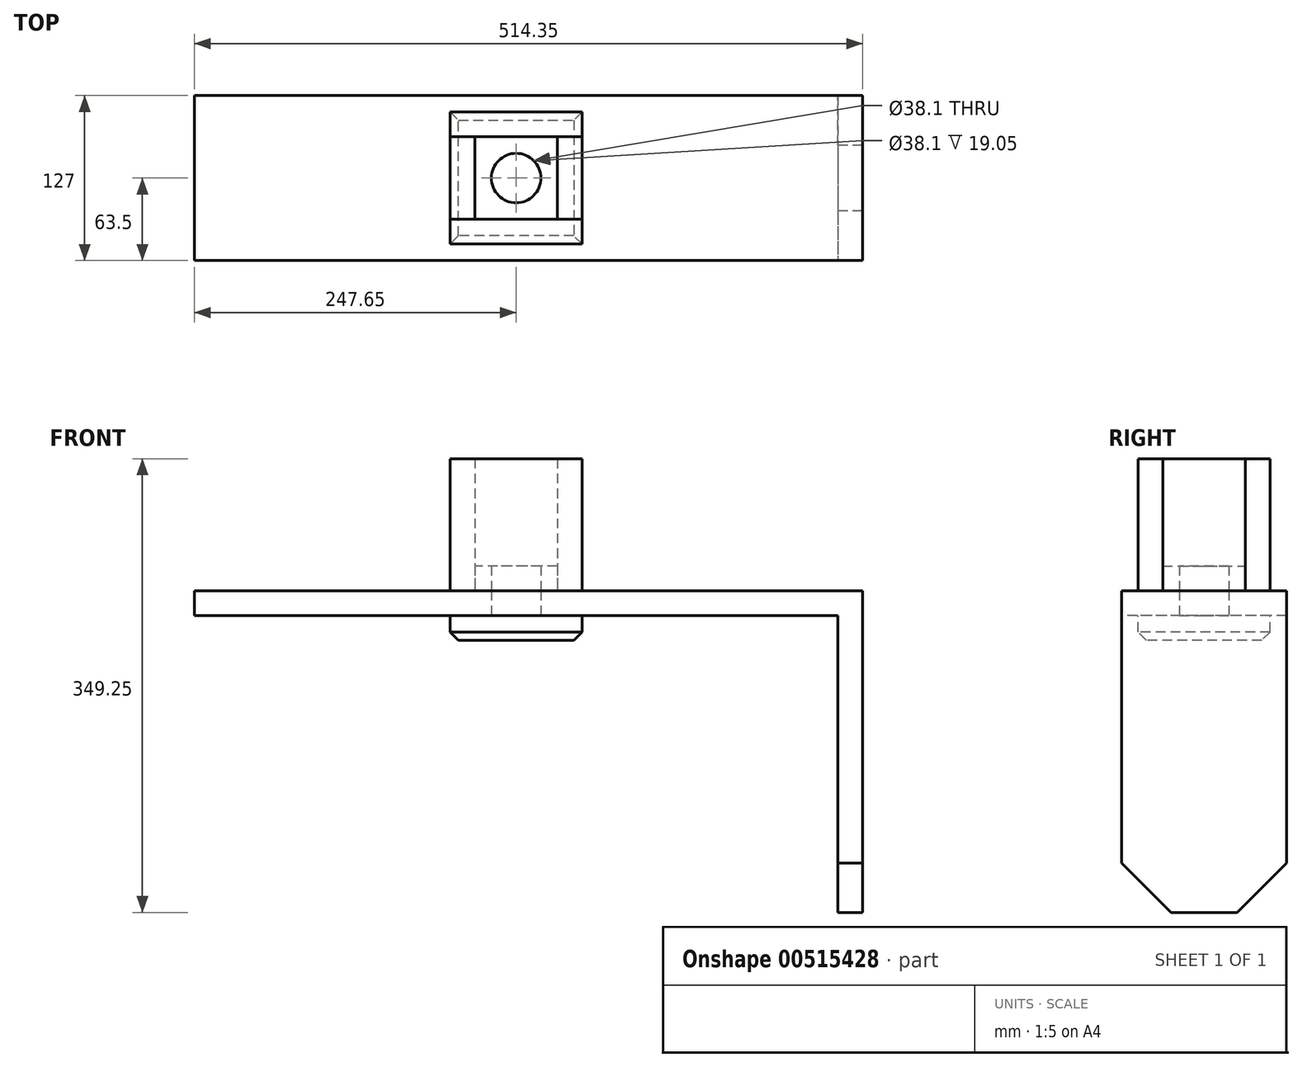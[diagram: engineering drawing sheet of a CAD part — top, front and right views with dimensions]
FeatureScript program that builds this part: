
annotation { "Feature Type Name" : "Feature", "Feature Type Description" : "" }
export const myFeature = defineFeature(function(context is Context, id is Id, definition is map)
    precondition{}
    {
        {
            var Q0;
            Q0=qCreatedBy(makeId("Top.planeOp"),FACE);
            var sketch = newSketch(context, id + "F0", { "sketchPlane" : qUnion([Q0])});
            skLineSegment(sketch, "E0.bottom", {"start": v(266.7, -63.5) * mm, "end": v(-266.7, -63.5) * mm});
            skLineSegment(sketch, "E0.top", {"start": v(266.7, 63.5) * mm, "end": v(-266.7, 63.5) * mm});
            skLineSegment(sketch, "E0.left", {"start": v(266.7, -63.5) * mm, "end": v(266.7, 63.5) * mm});
            skLineSegment(sketch, "E0.right", {"start": v(-266.7, -63.5) * mm, "end": v(-266.7, 63.5) * mm});
            skPoint(sketch, "E0.middle", {"position": v(0, 0) * mm});
            skLineSegment(sketch, "E1.bottom", {"start": v(-266.7, 63.5) * mm, "end": v(-247.65, 63.5) * mm});
            skLineSegment(sketch, "E1.top", {"start": v(-266.7, -63.5) * mm, "end": v(-247.65, -63.5) * mm});
            skLineSegment(sketch, "E1.left", {"start": v(-266.7, 63.5) * mm, "end": v(-266.7, -63.5) * mm});
            skLineSegment(sketch, "E1.right", {"start": v(-247.65, 63.5) * mm, "end": v(-247.65, -63.5) * mm});
            skLineSegment(sketch, "E2", {"start": v(0, 63.5) * mm, "end": v(0, -63.5) * mm, "construction": true});
            skLineSegment(sketch, "E3", {"start": v(-266.7, 0) * mm, "end": v(266.7, 0) * mm, "construction": true});
            skLineSegment(sketch, "E4.MirrorCS", {"start": v(247.65, 63.5) * mm, "end": v(247.65, -63.5) * mm});
            skSolve(sketch);
        }
        {
            var Q0;
            {var subQ0=sQuery(id+"F0.wireOp",EDGE,"E1.right");Q0=makeQuery(id+"F0.imprint","IMPRINT",FACE,{"disambiguationData":[TD([[makeQuery(id+"F0.imprint","IMPRINT",EDGE,{"derivedFrom":subQ0}),1.0]])]});}
            var Q1;
            Q1=makeQuery(id+"F0.imprint","IMPRINT",FACE,{"disambiguationData":[TD([[makeQuery(id+"F0.imprint","IMPRINT",EDGE,{"derivedFrom":sQuery(id+"F0.wireOp",EDGE,"E1.bottom")}),-1.0]])]});
            var Q2;
            {var subQ0=sQuery(id+"F0.wireOp",EDGE,"E0.left");Q2=makeQuery(id+"F0.imprint","IMPRINT",FACE,{"disambiguationData":[TD([[makeQuery(id+"F0.imprint","IMPRINT",EDGE,{"derivedFrom":subQ0}),1.0]])]});}
            extrude(context, id + "F1", {"entities" : qUnion([Q0, Q1, Q2]), "depth" : 19.05 * mm, "offsetDistance" : 25.4 * mm});
        }
        {
            var Q0;
            Q0=makeQuery(id+"F0.imprint","IMPRINT",FACE,{"disambiguationData":[TD([[makeQuery(id+"F0.imprint","IMPRINT",EDGE,{"derivedFrom":sQuery(id+"F0.wireOp",EDGE,"E1.bottom")}),-1.0]])]});
            var Q1;
            {var subQ0=sQuery(id+"F0.wireOp",EDGE,"E0.left");Q1=makeQuery(id+"F0.imprint","IMPRINT",FACE,{"disambiguationData":[TD([[makeQuery(id+"F0.imprint","IMPRINT",EDGE,{"derivedFrom":subQ0}),1.0]])]});}
            extrude(context, id + "F2", {"entities" : qUnion([Q0, Q1]), "operationType" : NewBodyOperationType.ADD, "oppositeDirection" : true, "depth" : 228.6 * mm, "offsetDistance" : 25.4 * mm});
        }
        {
            var Q0;
            Q0=makeQuery(id+"F2.opExtrude","CAP_EDGE",EDGE,{"disambiguationData":[OSD([sQuery(id+"F0.wireOp",EDGE,"E1.top")])],"isStart":false});
            var Q1;
            Q1=makeQuery(id+"F2.opExtrude","CAP_EDGE",EDGE,{"disambiguationData":[OSD([sQuery(id+"F0.wireOp",EDGE,"E1.bottom")])],"isStart":false});
            var Q2;
            Q2=makeQuery(id+"F2.opExtrude","CAP_EDGE",EDGE,{"disambiguationData":[OSD([sQuery(id+"F0.wireOp",EDGE,"E0.bottom")])],"isStart":false});
            var Q3;
            Q3=makeQuery(id+"F2.opExtrude","CAP_EDGE",EDGE,{"disambiguationData":[OSD([sQuery(id+"F0.wireOp",EDGE,"E0.top")])],"isStart":false});
            chamfer(context, id + "F3", {"entities" : qUnion([Q0, Q1, Q2, Q3]), "width" : 38.1 * mm, "tangentPropagation" : true});
        }
        {
            var Q0;
            Q0=makeQuery(id+"F1.opExtrude","CAP_FACE",FACE,{"disambiguationData":[OSD([sQuery(id+"F0.wireOp",EDGE,"E0.bottom"),sQuery(id+"F0.wireOp",EDGE,"E0.top"),sQuery(id+"F0.wireOp",EDGE,"E0.left"),sQuery(id+"F0.wireOp",EDGE,"E1.bottom"),sQuery(id+"F0.wireOp",EDGE,"E1.top"),sQuery(id+"F0.wireOp",EDGE,"E1.left")])],"isStart":false});
            var sketch = newSketch(context, id + "F4", { "sketchPlane" : qUnion([Q0])});
            skCircle(sketch, "E5", {"center": v(0, 0) * mm, "radius": 19.05 * mm});
            skLineSegment(sketch, "E6.bottom", {"start": v(31.75, -31.75) * mm, "end": v(-31.75, -31.75) * mm});
            skLineSegment(sketch, "E6.top", {"start": v(31.75, 31.75) * mm, "end": v(-31.75, 31.75) * mm});
            skLineSegment(sketch, "E6.left", {"start": v(31.75, -31.75) * mm, "end": v(31.75, 31.75) * mm});
            skLineSegment(sketch, "E6.right", {"start": v(-31.75, -31.75) * mm, "end": v(-31.75, 31.75) * mm});
            skLineSegment(sketch, "E7.bottom", {"start": v(-31.75, 31.75) * mm, "end": v(-50.8, 31.75) * mm});
            skLineSegment(sketch, "E7.top", {"start": v(-31.75, -31.75) * mm, "end": v(-50.8, -31.75) * mm});
            skLineSegment(sketch, "E7.left", {"start": v(-31.75, 31.75) * mm, "end": v(-31.75, -31.75) * mm});
            skLineSegment(sketch, "E7.right", {"start": v(-50.8, 31.75) * mm, "end": v(-50.8, -31.75) * mm});
            skLineSegment(sketch, "E8.MirrorCS", {"start": v(31.75, 31.75) * mm, "end": v(50.8, 31.75) * mm});
            skLineSegment(sketch, "E9.MirrorCS", {"start": v(50.8, 31.75) * mm, "end": v(50.8, -31.75) * mm});
            skLineSegment(sketch, "E10.MirrorCS", {"start": v(31.75, -31.75) * mm, "end": v(50.8, -31.75) * mm});
            skLineSegment(sketch, "E11.bottom", {"start": v(-50.8, 31.75) * mm, "end": v(50.8, 31.75) * mm});
            skLineSegment(sketch, "E11.top", {"start": v(-50.8, 50.8) * mm, "end": v(50.8, 50.8) * mm});
            skLineSegment(sketch, "E11.left", {"start": v(-50.8, 31.75) * mm, "end": v(-50.8, 50.8) * mm});
            skLineSegment(sketch, "E11.right", {"start": v(50.8, 31.75) * mm, "end": v(50.8, 50.8) * mm});
            skLineSegment(sketch, "E12.MirrorCS", {"start": v(-50.8, -31.75) * mm, "end": v(-50.8, -50.8) * mm});
            skLineSegment(sketch, "E13.MirrorCS", {"start": v(-50.8, -50.8) * mm, "end": v(50.8, -50.8) * mm});
            skLineSegment(sketch, "E14.MirrorCS", {"start": v(50.8, -31.75) * mm, "end": v(50.8, -50.8) * mm});
            skSolve(sketch);
        }
        {
            var Q0;
            Q0=makeQuery(id+"F4.imprint","IMPRINT",FACE,{"disambiguationData":[TD([[makeQuery(id+"F4.imprint","IMPRINT",EDGE,{"derivedFrom":sQuery(id+"F4.wireOp",EDGE,"E5")}),-1.0]])]});
            extrude(context, id + "F5", {"entities" : qUnion([Q0]), "depth" : 19.05 * mm, "offsetDistance" : 25.4 * mm});
        }
        {
            var Q0;
            Q0=makeQuery(id+"F4.imprint","IMPRINT",FACE,{"disambiguationData":[TD([[makeQuery(id+"F4.imprint","IMPRINT",EDGE,{"derivedFrom":sQuery(id+"F4.wireOp",EDGE,"E11.top")}),-1.0]])]});
            var Q1;
            Q1=makeQuery(id+"F4.imprint","IMPRINT",FACE,{"disambiguationData":[TD([[makeQuery(id+"F4.imprint","IMPRINT",EDGE,{"derivedFrom":sQuery(id+"F4.wireOp",EDGE,"E6.bottom")}),1.0]])]});
            extrude(context, id + "F6", {"entities" : qUnion([Q0, Q1]), "depth" : 101.6 * mm, "offsetDistance" : 25.4 * mm});
        }
        {
            var Q0;
            Q0=makeQuery(id+"F4.imprint","IMPRINT",FACE,{"disambiguationData":[TD([[makeQuery(id+"F4.imprint","IMPRINT",EDGE,{"derivedFrom":sQuery(id+"F4.wireOp",EDGE,"E7.top")}),-1.0]])]});
            var Q1;
            {var subQ0=sQuery(id+"F4.wireOp",EDGE,"E6.left");Q1=makeQuery(id+"F4.imprint","IMPRINT",FACE,{"disambiguationData":[TD([[makeQuery(id+"F4.imprint","IMPRINT",EDGE,{"derivedFrom":subQ0}),-1.0]])]});}
            extrude(context, id + "F7", {"entities" : qUnion([Q0, Q1]), "depth" : 101.6 * mm, "offsetDistance" : 25.4 * mm});
        }
        {
            var Q0;
            {var subQ0=sQuery(id+"F0.wireOp",EDGE,"E1.right");Q0=makeQuery(id+"F0.imprint","IMPRINT",FACE,{"disambiguationData":[TD([[makeQuery(id+"F0.imprint","IMPRINT",EDGE,{"derivedFrom":subQ0}),1.0]])]});}
            var sketch = newSketch(context, id + "F8", { "sketchPlane" : qUnion([Q0])});
            skLineSegment(sketch, "E15.0", {"start": v(-50.8, -50.8) * mm, "end": v(50.8, -50.8) * mm});
            skLineSegment(sketch, "E15.1", {"start": v(-50.8, -31.75) * mm, "end": v(-50.8, -50.8) * mm});
            skLineSegment(sketch, "E15.2", {"start": v(-50.8, 31.75) * mm, "end": v(-50.8, -31.75) * mm});
            skLineSegment(sketch, "E15.3", {"start": v(-50.8, 31.75) * mm, "end": v(-50.8, 50.8) * mm});
            skLineSegment(sketch, "E15.4", {"start": v(-50.8, 50.8) * mm, "end": v(50.8, 50.8) * mm});
            skLineSegment(sketch, "E15.5", {"start": v(50.8, 31.75) * mm, "end": v(50.8, 50.8) * mm});
            skLineSegment(sketch, "E15.6", {"start": v(50.8, 31.75) * mm, "end": v(50.8, -31.75) * mm});
            skLineSegment(sketch, "E15.7", {"start": v(50.8, -31.75) * mm, "end": v(50.8, -50.8) * mm});
            skCircle(sketch, "E15.8", {"center": v(0, 0) * mm, "radius": 19.05 * mm});
            skSolve(sketch);
        }
        {
            var Q0;
            Q0=makeQuery(id+"F8.imprint","IMPRINT",FACE,{"disambiguationData":[TD([[makeQuery(id+"F8.imprint","IMPRINT",EDGE,{"derivedFrom":sQuery(id+"F8.wireOp",EDGE,"E15.8")}),1.0]])]});
            extrude(context, id + "F9", {"entities" : qUnion([Q0]), "operationType" : NewBodyOperationType.REMOVE, "depth" : 19.05 * mm, "offsetDistance" : 25.4 * mm});
        }
        {
            var Q0;
            Q0=makeQuery(id+"F8.imprint","IMPRINT",FACE,{"disambiguationData":[TD([[makeQuery(id+"F8.imprint","IMPRINT",EDGE,{"derivedFrom":sQuery(id+"F8.wireOp",EDGE,"E15.0")}),1.0]])]});
            var Q1;
            Q1=makeQuery(id+"F8.imprint","IMPRINT",FACE,{"disambiguationData":[TD([[makeQuery(id+"F8.imprint","IMPRINT",EDGE,{"derivedFrom":sQuery(id+"F8.wireOp",EDGE,"E15.8")}),1.0]])]});
            extrude(context, id + "F10", {"entities" : qUnion([Q0, Q1]), "operationType" : NewBodyOperationType.ADD, "oppositeDirection" : true, "depth" : 19.05 * mm, "offsetDistance" : 25.4 * mm});
        }
        {
            var Q0;
            Q0=makeQuery(id+"F10.opExtrude","CAP_FACE",FACE,{"disambiguationData":[OSD([sQuery(id+"F8.wireOp",EDGE,"E15.0"),sQuery(id+"F8.wireOp",EDGE,"E15.1"),sQuery(id+"F8.wireOp",EDGE,"E15.2"),sQuery(id+"F8.wireOp",EDGE,"E15.3"),sQuery(id+"F8.wireOp",EDGE,"E15.4"),sQuery(id+"F8.wireOp",EDGE,"E15.5"),sQuery(id+"F8.wireOp",EDGE,"E15.6"),sQuery(id+"F8.wireOp",EDGE,"E15.7")])],"isStart":false});
            chamfer(context, id + "F11", {"entities" : qUnion([Q0]), "width" : 6.35 * mm, "tangentPropagation" : true});
        }
    });
